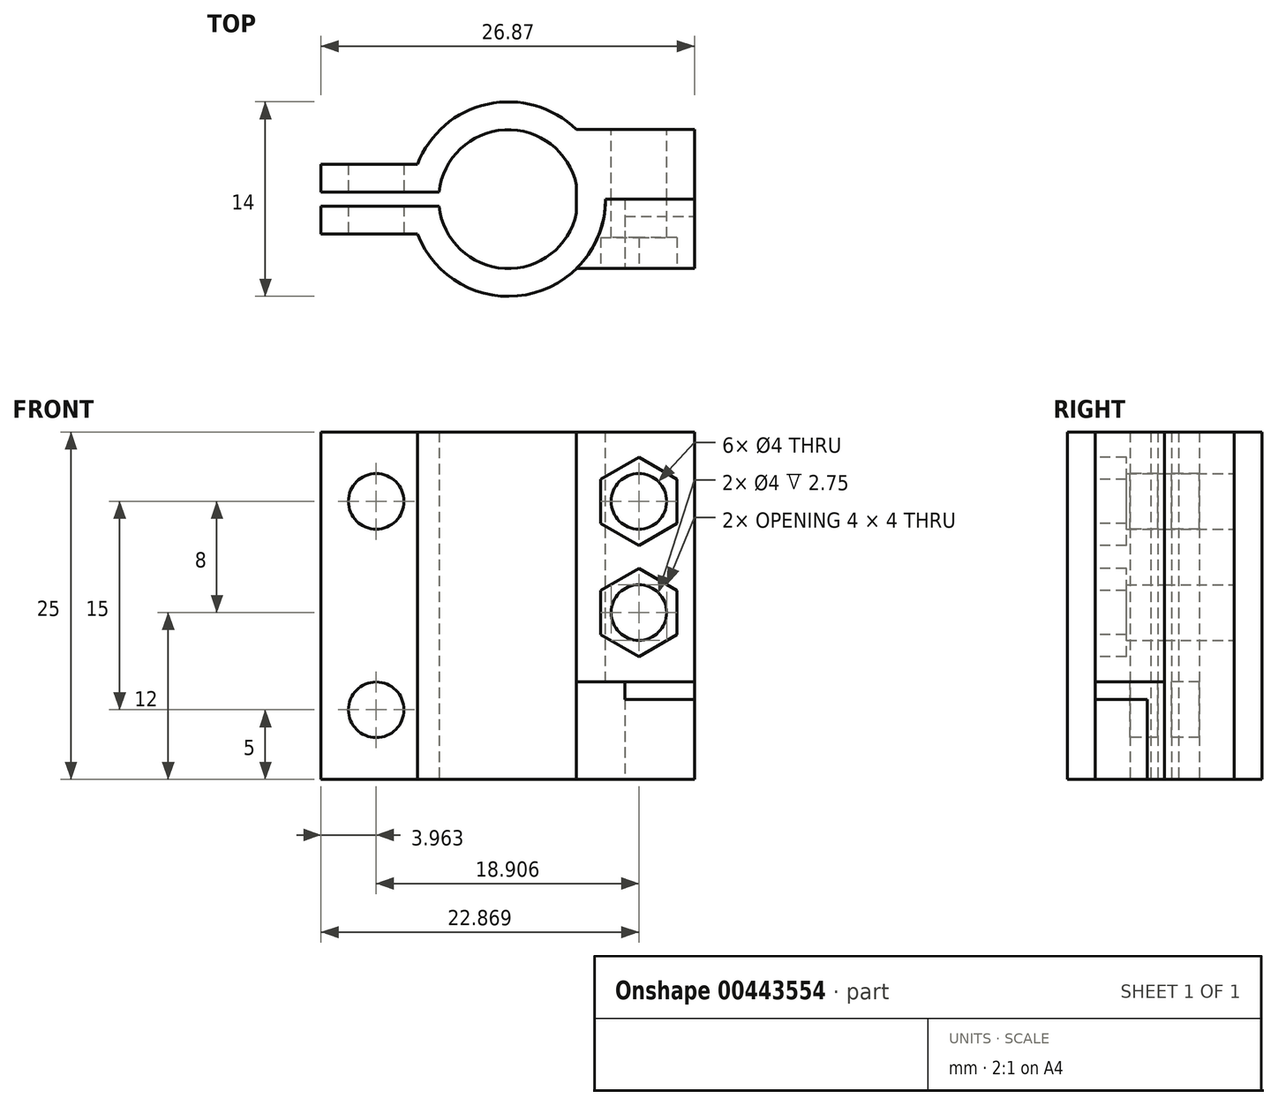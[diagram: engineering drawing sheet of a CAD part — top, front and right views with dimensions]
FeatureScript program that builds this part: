
annotation { "Feature Type Name" : "Feature", "Feature Type Description" : "" }
export const myFeature = defineFeature(function(context is Context, id is Id, definition is map)
    precondition{}
    {
        {
            var Q0;
            Q0=qCreatedBy(makeId("Top.planeOp"),FACE);
            var sketch = newSketch(context, id + "F0", { "sketchPlane" : qUnion([Q0])});
            skCircle(sketch, "E0", {"center": v(0, 0) * mm, "radius": 5 * mm});
            skCircle(sketch, "E1", {"center": v(0, 0) * mm, "radius": 7 * mm});
            skSolve(sketch);
        }
        {
            var Q0;
            Q0=qSketchRegion(id+"F0",true);
            extrude(context, id + "F1", {"entities" : qUnion([Q0]), "depth" : 25 * mm});
        }
        {
            var Q0;
            Q0=qCreatedBy(makeId("Right.planeOp"),FACE);
            var sketch = newSketch(context, id + "F2", { "sketchPlane" : qUnion([Q0])});
            skLineSegment(sketch, "E2", {"start": v(0, 25) * mm, "end": v(0, 0) * mm, "construction": true});
            skLineSegment(sketch, "E3.bottom", {"start": v(0.5, 25) * mm, "end": v(-0.5, 25) * mm});
            skLineSegment(sketch, "E3.top", {"start": v(0.5, 0) * mm, "end": v(-0.5, 0) * mm});
            skLineSegment(sketch, "E3.left", {"start": v(0.5, 25) * mm, "end": v(0.5, 0) * mm});
            skLineSegment(sketch, "E3.right", {"start": v(-0.5, 25) * mm, "end": v(-0.5, 0) * mm});
            skPoint(sketch, "E3.middle", {"position": v(0, 12.5) * mm});
            skSolve(sketch);
        }
        {
            var Q0;
            Q0=qSketchRegion(id+"F2",true);
            extrude(context, id + "F3", {"entities" : qUnion([Q0]), "operationType" : NewBodyOperationType.REMOVE, "oppositeDirection" : true, "depth" : 25 * mm});
        }
        {
            var Q0;
            Q0=makeQuery(id+"F3.boolean.opBoolean","COPY",FACE,{"derivedFrom":makeQuery(id+"F3.opExtrude","SWEPT_FACE",FACE,{"disambiguationData":[OSD([sQuery(id+"F2.wireOp",EDGE,"E3.right")])]})});
            var sketch = newSketch(context, id + "F4", { "sketchPlane" : qUnion([Q0])});
            skPoint(sketch, "E4.oppositeSnap0", {"position": v(5.98, 0) * mm});
            skLineSegment(sketch, "E4.bottom", {"start": v(4.97, 25) * mm, "end": v(12.47, 25) * mm});
            skLineSegment(sketch, "E4.top", {"start": v(4.97, 0) * mm, "end": v(12.47, 0) * mm});
            skLineSegment(sketch, "E4.left", {"start": v(4.97, 25) * mm, "end": v(4.97, 0) * mm});
            skLineSegment(sketch, "E4.right", {"start": v(12.47, 25) * mm, "end": v(12.47, 0) * mm});
            skSolve(sketch);
        }
        {
            var Q0;
            Q0=qSketchRegion(id+"F4",true);
            extrude(context, id + "F5", {"entities" : qUnion([Q0]), "oppositeDirection" : true, "depth" : 2 * mm});
        }
        {
            var Q0;
            Q0=makeQuery(id+"F5.opExtrude","SWEPT_BODY",BODY,{"disambiguationData":[OSD([sQuery(id+"F4.wireOp",EDGE,"E4.bottom"),sQuery(id+"F4.wireOp",EDGE,"E4.top"),sQuery(id+"F4.wireOp",EDGE,"E4.left"),sQuery(id+"F4.wireOp",EDGE,"E4.right")])]});
            var Q1;
            Q1=qCreatedBy(makeId("Front.planeOp"),FACE);
            mirror(context, id + "F6", {"operationType" : NewBodyOperationType.ADD, "entities" : qUnion([Q0]), "mirrorPlane" : qUnion([Q1])});
        }
        {
            var Q0;
            {var subQ0=makeQuery(id+"F5.opExtrude","SWEPT_FACE",FACE,{"disambiguationData":[OSD([sQuery(id+"F4.wireOp",EDGE,"E4.bottom")])]});Q0=makeQuery(id+"F6.boolean.opBoolean","MERGE",FACE,{"derivedFrom":[makeQuery(id+"F1.opExtrude","CAP_FACE",FACE,{"disambiguationData":[OSD([sQuery(id+"F0.wireOp",EDGE,"E0"),sQuery(id+"F0.wireOp",EDGE,"E1")])],"isStart":false}),subQ0,makeQuery(id+"F6.opPattern","COPY",FACE,{"derivedFrom":subQ0,"instanceName":"1"})]});}
            var sketch = newSketch(context, id + "F7", { "sketchPlane" : qUnion([Q0])});
            skLineSegment(sketch, "E5.bottom", {"start": v(4.9, 5) * mm, "end": v(9.9, 5) * mm});
            skLineSegment(sketch, "E5.top", {"start": v(4.9, -5) * mm, "end": v(9.9, -5) * mm});
            skLineSegment(sketch, "E5.left", {"start": v(4.9, 5) * mm, "end": v(4.9, -5) * mm});
            skLineSegment(sketch, "E5.right", {"start": v(9.9, 5) * mm, "end": v(9.9, -5) * mm});
            skSolve(sketch);
        }
        {
            var Q0;
            Q0=qSketchRegion(id+"F7",true);
            extrude(context, id + "F8", {"entities" : qUnion([Q0]), "operationType" : NewBodyOperationType.ADD, "oppositeDirection" : true, "depth" : 25 * mm});
        }
        {
            var Q0;
            {var subQ0=makeQuery(id+"F5.opExtrude","SWEPT_FACE",FACE,{"disambiguationData":[OSD([sQuery(id+"F4.wireOp",EDGE,"E4.bottom")])]});Q0=makeQuery(id+"F8.boolean.opBoolean","MERGE",FACE,{"derivedFrom":[makeQuery(id+"F6.boolean.opBoolean","MERGE",FACE,{"derivedFrom":[makeQuery(id+"F1.opExtrude","CAP_FACE",FACE,{"disambiguationData":[OSD([sQuery(id+"F0.wireOp",EDGE,"E0"),sQuery(id+"F0.wireOp",EDGE,"E1")])],"isStart":false}),subQ0,makeQuery(id+"F6.opPattern","COPY",FACE,{"derivedFrom":subQ0,"instanceName":"1"})]}),makeQuery(id+"F8.opExtrude","CAP_FACE",FACE,{"disambiguationData":[OSD([sQuery(id+"F7.wireOp",EDGE,"E5.bottom"),sQuery(id+"F7.wireOp",EDGE,"E5.top"),sQuery(id+"F7.wireOp",EDGE,"E5.left"),sQuery(id+"F7.wireOp",EDGE,"E5.right")])],"isStart":true})]});}
            var sketch = newSketch(context, id + "F9", { "sketchPlane" : qUnion([Q0])});
            skArc(sketch, "E6", {"start": v(4.9, -5) * mm, "mid": v(6.06, -3.5) * mm, "end": v(6.78, -1.75) * mm});
            skLineSegment(sketch, "E7.0", {"start": v(9.9, 0) * mm, "end": v(9.9, -5) * mm});
            skLineSegment(sketch, "E8.0", {"start": v(4.9, -5) * mm, "end": v(9.9, -5) * mm});
            skLineSegment(sketch, "E9", {"start": v(6.78, -1.75) * mm, "end": v(9.9, 0) * mm});
            skSolve(sketch);
        }
        {
            var Q0;
            Q0=qSketchRegion(id+"F9",true);
            extrude(context, id + "F10", {"entities" : qUnion([Q0]), "operationType" : NewBodyOperationType.REMOVE, "oppositeDirection" : true, "depth" : 18 * mm});
        }
        {
            var Q0;
            {var subQ0=sQuery(id+"F7.wireOp",EDGE,"E5.right");var subQ4=makeQuery(id+"F5.opExtrude","SWEPT_FACE",FACE,{"disambiguationData":[OSD([sQuery(id+"F4.wireOp",EDGE,"E4.bottom")])]});Q0=makeQuery(id+"FAku0vlT2cx2uVS_1.boolean.opBoolean","SPLIT",FACE,{"disambiguationData":[TD([subQ4])],"derivedFrom":makeQuery(id+"F8.opExtrude","SWEPT_FACE",FACE,{"disambiguationData":[OSD([subQ0])]})});}
            var Q1;
            {var subQ0=sQuery(id+"F7.wireOp",EDGE,"E5.right");var subQ1=sQuery(id+"F7.wireOp",EDGE,"E5.top");Q1=makeQuery(id+"FAku0vlT2cx2uVS_1.boolean.opBoolean","SPLIT",FACE,{"disambiguationData":[TD([makeQuery(id+"F8.opExtrude","SWEPT_FACE",FACE,{"disambiguationData":[OSD([subQ1])]})])],"derivedFrom":makeQuery(id+"F8.opExtrude","SWEPT_FACE",FACE,{"disambiguationData":[OSD([subQ0])]})});}
            extrude(context, id + "F11", {"entities" : qUnion([Q0, Q1]), "operationType" : NewBodyOperationType.ADD, "depth" : 2.5 * mm});
        }
        {
            var Q0;
            {var subQ0=sQuery(id+"F7.wireOp",EDGE,"E5.right");var subQ1=makeQuery(id+"F5.opExtrude","SWEPT_FACE",FACE,{"disambiguationData":[OSD([sQuery(id+"F4.wireOp",EDGE,"E4.bottom")])]});Q0=makeQuery(id+"F11.boolean.opBoolean","MERGE",FACE,{"derivedFrom":[makeQuery(id+"F8.boolean.opBoolean","MERGE",FACE,{"derivedFrom":[makeQuery(id+"F6.boolean.opBoolean","MERGE",FACE,{"derivedFrom":[makeQuery(id+"F1.opExtrude","CAP_FACE",FACE,{"disambiguationData":[OSD([sQuery(id+"F0.wireOp",EDGE,"E0"),sQuery(id+"F0.wireOp",EDGE,"E1")])],"isStart":false}),subQ1,makeQuery(id+"F6.opPattern","COPY",FACE,{"derivedFrom":subQ1,"instanceName":"1"})]}),makeQuery(id+"F8.opExtrude","CAP_FACE",FACE,{"disambiguationData":[OSD([sQuery(id+"F7.wireOp",EDGE,"E5.bottom"),sQuery(id+"F7.wireOp",EDGE,"E5.top"),sQuery(id+"F7.wireOp",EDGE,"E5.left"),subQ0])],"isStart":true})]}),makeQuery(id+"F11.opExtrude","SWEPT_FACE",FACE,{"disambiguationData":[OSD([subQ0]),TDD([makeQuery(id+"F8.opExtrude","CAP_EDGE",EDGE,{"disambiguationData":[OSD([subQ0])],"isStart":true})])]})]});}
            var sketch = newSketch(context, id + "F12", { "sketchPlane" : qUnion([Q0])});
            skLineSegment(sketch, "E10.0", {"start": v(6.78, -1.75) * mm, "end": v(9.9, 0) * mm});
            skArc(sketch, "E11", {"start": v(6.78, -1.75) * mm, "mid": v(6.94, -0.88) * mm, "end": v(7, 0) * mm});
            skLineSegment(sketch, "E12", {"start": v(7, 0) * mm, "end": v(9.9, 0) * mm});
            skSolve(sketch);
        }
        {
            var Q0;
            Q0 = qSketchRegion(id + "F12", true);
            extrude(context, id + "F13", {"entities" : qUnion([Q0]), "operationType" : NewBodyOperationType.REMOVE, "oppositeDirection" : true, "depth" : 18 * mm});
        }
        {
            var Q0;
            Q0=makeQuery(id+"F11.opExtrude","CAP_FACE",FACE,{"disambiguationData":[OSD([sQuery(id+"F7.wireOp",EDGE,"E5.right")])],"isStart":false});
            extrude(context, id + "F14", {"entities" : qUnion([Q0]), "operationType" : NewBodyOperationType.ADD, "depth" : 1 * mm});
        }
        {
            var Q0;
            Q0=makeQuery(id+"F14.opExtrude","CAP_FACE",FACE,{"disambiguationData":[OSD([sQuery(id+"F7.wireOp",EDGE,"E5.right")])],"isStart":false});
            var sketch = newSketch(context, id + "F15", { "sketchPlane" : qUnion([Q0])});
            skLineSegment(sketch, "E13.0", {"start": v(-1.25, 5.75) * mm, "end": v(-5, 5.75) * mm});
            skLineSegment(sketch, "E14.0", {"start": v(0, 7) * mm, "end": v(0, 0) * mm});
            skLineSegment(sketch, "E15.0", {"start": v(-5, 5.75) * mm, "end": v(-5, 7) * mm});
            skLineSegment(sketch, "E16", {"start": v(0, 0) * mm, "end": v(-1.25, 0) * mm});
            skLineSegment(sketch, "E17.0", {"start": v(0, 7) * mm, "end": v(-5, 7) * mm});
            skLineSegment(sketch, "E18", {"start": v(-5, 0) * mm, "end": v(0, 0) * mm, "construction": true});
            skLineSegment(sketch, "E19", {"start": v(-1.25, 5.75) * mm, "end": v(-1.25, 0) * mm});
            skSolve(sketch);
        }
        {
            var Q0;
            Q0 = qSketchRegion(id + "F15", true);
            extrude(context, id + "F16", {"entities" : qUnion([Q0]), "operationType" : NewBodyOperationType.REMOVE, "oppositeDirection" : true, "depth" : 5 * mm});
        }
        {
            var Q0;
            {var subQ0=sQuery(id+"F7.wireOp",EDGE,"E5.right");var subQ1=sQuery(id+"F7.wireOp",EDGE,"E5.bottom");Q0=makeQuery(id+"F14.boolean.opBoolean","MERGE",FACE,{"derivedFrom":[makeQuery(id+"F11.boolean.opBoolean","MERGE",FACE,{"derivedFrom":[makeQuery(id+"F8.opExtrude","SWEPT_FACE",FACE,{"disambiguationData":[OSD([subQ1])]}),makeQuery(id+"F11.opExtrude","SWEPT_FACE",FACE,{"disambiguationData":[OSD([subQ1,subQ0])]})]}),makeQuery(id+"F14.opExtrude","SWEPT_FACE",FACE,{"disambiguationData":[OSD([subQ1,subQ0])]})]});}
            var sketch = newSketch(context, id + "F17", { "sketchPlane" : qUnion([Q0])});
            skLineSegment(sketch, "E20", {"start": v(-9.4, 25) * mm, "end": v(-9.4, 0) * mm, "construction": true});
            skCircle(sketch, "E21", {"center": v(-9.4, 20) * mm, "radius": 2 * mm});
            skCircle(sketch, "E22", {"center": v(-9.4, 12) * mm, "radius": 2 * mm});
            skLineSegment(sketch, "E23", {"start": v(-9.4, 0) * mm, "end": v(0, 0) * mm, "construction": true});
            skSolve(sketch);
        }
        {
            var Q0;
            Q0 = qSketchRegion(id + "F17", true);
            extrude(context, id + "F18", {"entities" : qUnion([Q0]), "operationType" : NewBodyOperationType.REMOVE, "endBound" : BoundingType.THROUGH_ALL, "oppositeDirection" : true, "depth" : 25 * mm});
        }
        {
            var Q0;
            Q0=makeQuery(id+"F5.opExtrude","CAP_FACE",FACE,{"disambiguationData":[OSD([sQuery(id+"F4.wireOp",EDGE,"E4.bottom"),sQuery(id+"F4.wireOp",EDGE,"E4.top"),sQuery(id+"F4.wireOp",EDGE,"E4.left"),sQuery(id+"F4.wireOp",EDGE,"E4.right")])],"isStart":false});
            var sketch = newSketch(context, id + "F19", { "sketchPlane" : qUnion([Q0])});
            skLineSegment(sketch, "E24", {"start": v(-9.5, 25) * mm, "end": v(-9.5, 0) * mm, "construction": true});
            skCircle(sketch, "E25", {"center": v(-9.5, 20) * mm, "radius": 2 * mm});
            skCircle(sketch, "E26", {"center": v(-9.5, 5) * mm, "radius": 2 * mm});
            skSolve(sketch);
        }
        {
            var Q0;
            Q0 = qSketchRegion(id + "F19", true);
            extrude(context, id + "F20", {"entities" : qUnion([Q0]), "operationType" : NewBodyOperationType.REMOVE, "endBound" : BoundingType.THROUGH_ALL, "oppositeDirection" : true, "depth" : 25 * mm});
        }
        {
            var Q0;
            {var subQ0=sQuery(id+"F7.wireOp",EDGE,"E5.right");var subQ1=makeQuery(id+"F8.opExtrude","CAP_EDGE",EDGE,{"disambiguationData":[OSD([subQ0])],"isStart":true});var subQ2=makeQuery(id+"F5.opExtrude","SWEPT_FACE",FACE,{"disambiguationData":[OSD([sQuery(id+"F4.wireOp",EDGE,"E4.bottom")])]});Q0=makeQuery(id+"F14.boolean.opBoolean","MERGE",FACE,{"derivedFrom":[makeQuery(id+"F11.boolean.opBoolean","MERGE",FACE,{"derivedFrom":[makeQuery(id+"F8.boolean.opBoolean","MERGE",FACE,{"derivedFrom":[makeQuery(id+"F6.boolean.opBoolean","MERGE",FACE,{"derivedFrom":[makeQuery(id+"F1.opExtrude","CAP_FACE",FACE,{"disambiguationData":[OSD([sQuery(id+"F0.wireOp",EDGE,"E0"),sQuery(id+"F0.wireOp",EDGE,"E1")])],"isStart":false}),subQ2,makeQuery(id+"F6.opPattern","COPY",FACE,{"derivedFrom":subQ2,"instanceName":"1"})]}),makeQuery(id+"F8.opExtrude","CAP_FACE",FACE,{"disambiguationData":[OSD([sQuery(id+"F7.wireOp",EDGE,"E5.bottom"),sQuery(id+"F7.wireOp",EDGE,"E5.top"),sQuery(id+"F7.wireOp",EDGE,"E5.left"),subQ0])],"isStart":true})]}),makeQuery(id+"F11.opExtrude","SWEPT_FACE",FACE,{"disambiguationData":[OSD([subQ0]),TDD([subQ1])]})]}),makeQuery(id+"F14.opExtrude","SWEPT_FACE",FACE,{"disambiguationData":[OSD([subQ0]),TDD([makeQuery(id+"F11.opExtrude","CAP_EDGE",EDGE,{"disambiguationData":[OSD([subQ0]),TDD([subQ1])],"isStart":false})])]})]});}
            var sketch = newSketch(context, id + "F21", { "sketchPlane" : qUnion([Q0])});
            skLineSegment(sketch, "E27.0", {"start": v(13.4, 0) * mm, "end": v(7, 0) * mm});
            skArc(sketch, "E28.0", {"start": v(-6.54, -2.5) * mm, "mid": v(1.27, -6.88) * mm, "end": v(7, 0) * mm});
            skLineSegment(sketch, "E29.0", {"start": v(4.9, -5) * mm, "end": v(13.4, -5) * mm});
            skLineSegment(sketch, "E30", {"start": v(13.4, 0) * mm, "end": v(13.4, -5) * mm});
            skSolve(sketch);
        }
        {
            var Q0;
            Q0 = qSketchRegion(id + "F21", true);
            extrude(context, id + "F22", {"entities" : qUnion([Q0]), "oppositeDirection" : true, "depth" : 18 * mm});
        }
        {
            var Q0;
            Q0=makeQuery(id+"F22.opExtrude","SWEPT_FACE",FACE,{"disambiguationData":[OSD([sQuery(id+"F21.wireOp",EDGE,"E27.0")])]});
            var sketch = newSketch(context, id + "F23", { "sketchPlane" : qUnion([Q0])});
            skCircle(sketch, "E31.0", {"center": v(-9.4, 20) * mm, "radius": 2 * mm});
            skCircle(sketch, "E32.0", {"center": v(-9.4, 12) * mm, "radius": 2 * mm});
            skSolve(sketch);
        }
        {
            var Q0;
            Q0 = qSketchRegion(id + "F23", true);
            extrude(context, id + "F24", {"entities" : qUnion([Q0]), "operationType" : NewBodyOperationType.REMOVE, "endBound" : BoundingType.THROUGH_ALL, "oppositeDirection" : true, "depth" : 25 * mm});
        }
        {
            var Q0;
            Q0=makeQuery(id+"F22.opExtrude","SWEPT_FACE",FACE,{"disambiguationData":[OSD([sQuery(id+"F21.wireOp",EDGE,"E29.0")])]});
            var sketch = newSketch(context, id + "F25", { "sketchPlane" : qUnion([Q0])});
            skCircle(sketch, "E33.cCircle", {"center": v(9.4, 20) * mm, "radius": 2.75 * mm, "construction": true});
            skLineSegment(sketch, "E33.0", {"start": v(6.65, 21.59) * mm, "end": v(9.4, 23.18) * mm});
            skLineSegment(sketch, "E33.1", {"start": v(9.4, 23.18) * mm, "end": v(12.15, 21.59) * mm});
            skLineSegment(sketch, "E33.2", {"start": v(12.15, 21.59) * mm, "end": v(12.15, 18.41) * mm});
            skLineSegment(sketch, "E33.3", {"start": v(12.15, 18.41) * mm, "end": v(9.4, 16.82) * mm});
            skLineSegment(sketch, "E33.4", {"start": v(9.4, 16.82) * mm, "end": v(6.65, 18.41) * mm});
            skLineSegment(sketch, "E33.5", {"start": v(6.65, 18.41) * mm, "end": v(6.65, 21.59) * mm});
            skPoint(sketch, "E33.0.midPoint", {"position": v(8.02, 22.38) * mm});
            skCircle(sketch, "E34.cCircle", {"center": v(9.4, 12) * mm, "radius": 2.75 * mm, "construction": true});
            skLineSegment(sketch, "E34.0", {"start": v(6.65, 13.59) * mm, "end": v(9.4, 15.18) * mm});
            skLineSegment(sketch, "E34.1", {"start": v(9.4, 15.18) * mm, "end": v(12.15, 13.59) * mm});
            skLineSegment(sketch, "E34.2", {"start": v(12.15, 13.59) * mm, "end": v(12.15, 10.41) * mm});
            skLineSegment(sketch, "E34.3", {"start": v(12.15, 10.41) * mm, "end": v(9.4, 8.82) * mm});
            skLineSegment(sketch, "E34.4", {"start": v(9.4, 8.82) * mm, "end": v(6.65, 10.41) * mm});
            skLineSegment(sketch, "E34.5", {"start": v(6.65, 10.41) * mm, "end": v(6.65, 13.59) * mm});
            skPoint(sketch, "E34.0.midPoint", {"position": v(8.02, 14.38) * mm});
            skSolve(sketch);
        }
        {
            var Q0;
            Q0 = qSketchRegion(id + "F25", true);
            extrude(context, id + "F26", {"entities" : qUnion([Q0]), "operationType" : NewBodyOperationType.REMOVE, "oppositeDirection" : true, "depth" : 2.25 * mm});
        }
        {
            var Q0;
            Q0=makeQuery(id+"F6.opPattern","COPY",FACE,{"derivedFrom":makeQuery(id+"F5.opExtrude","SWEPT_FACE",FACE,{"disambiguationData":[OSD([sQuery(id+"F4.wireOp",EDGE,"E4.right")])]}),"instanceName":"1"});
            var Q1;
            Q1=makeQuery(id+"F5.opExtrude","SWEPT_FACE",FACE,{"disambiguationData":[OSD([sQuery(id+"F4.wireOp",EDGE,"E4.right")])]});
            extrude(context, id + "F27", {"entities" : qUnion([Q0, Q1]), "operationType" : NewBodyOperationType.ADD, "depth" : 1 * mm});
        }
    });
